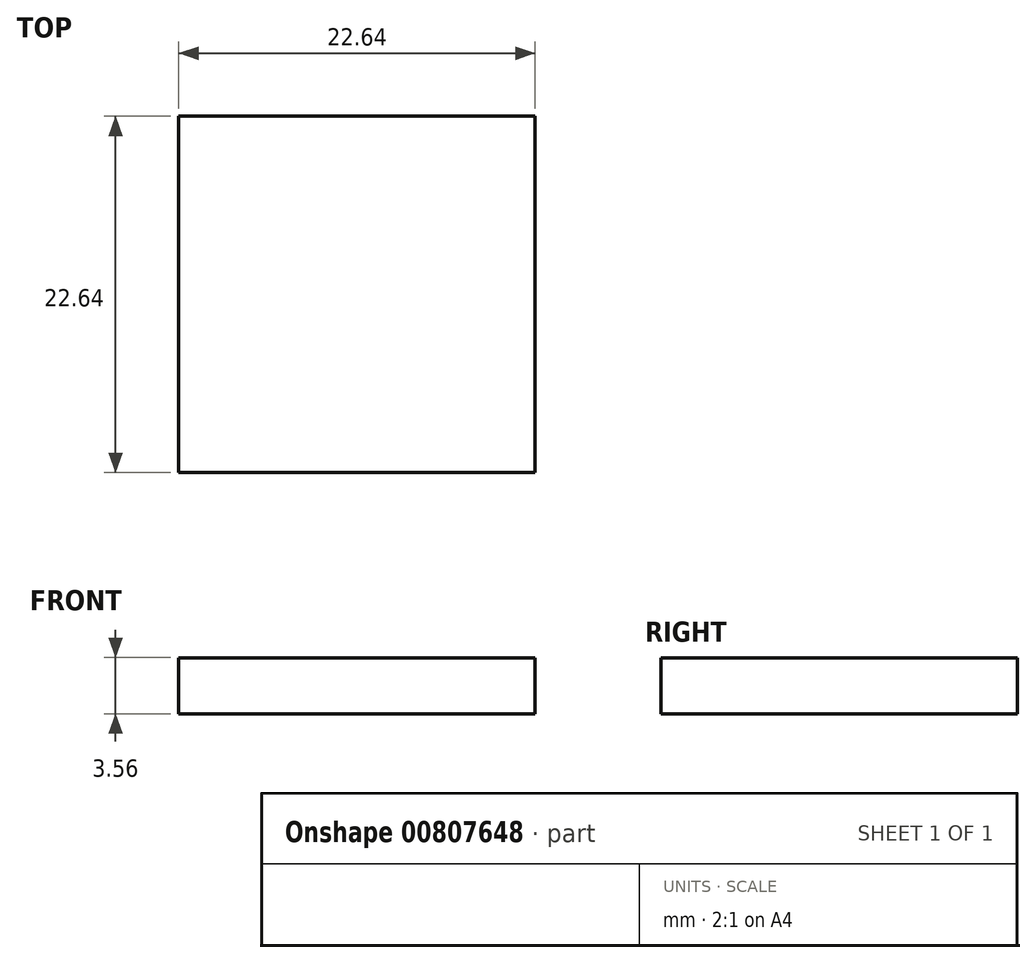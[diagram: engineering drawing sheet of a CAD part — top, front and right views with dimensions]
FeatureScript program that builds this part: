
annotation { "Feature Type Name" : "Feature", "Feature Type Description" : "" }
export const myFeature = defineFeature(function(context is Context, id is Id, definition is map)
    precondition{}
    {
        {
            var Q0;
            Q0=qCreatedBy(makeId("Top.planeOp"),FACE);
            var sketch = newSketch(context, id + "F0", { "sketchPlane" : qUnion([Q0])});
            skLineSegment(sketch, "E0.bottom", {"start": v(11.32, 11.32) * mm, "end": v(-11.32, 11.32) * mm});
            skLineSegment(sketch, "E0.top", {"start": v(11.32, -11.32) * mm, "end": v(-11.32, -11.32) * mm});
            skLineSegment(sketch, "E0.left", {"start": v(11.32, 11.32) * mm, "end": v(11.32, -11.32) * mm});
            skLineSegment(sketch, "E0.right", {"start": v(-11.32, 11.32) * mm, "end": v(-11.32, -11.32) * mm});
            skPoint(sketch, "E0.middle", {"position": v(0, 0) * mm});
            skSolve(sketch);
        }
        {
            var Q0;
            Q0 = qSketchRegion(id + "F0", true);
            extrude(context, id + "F1", {"entities" : qUnion([Q0]), "depth" : 3.56 * mm, "offsetDistance" : 25.4 * mm});
        }
    });
